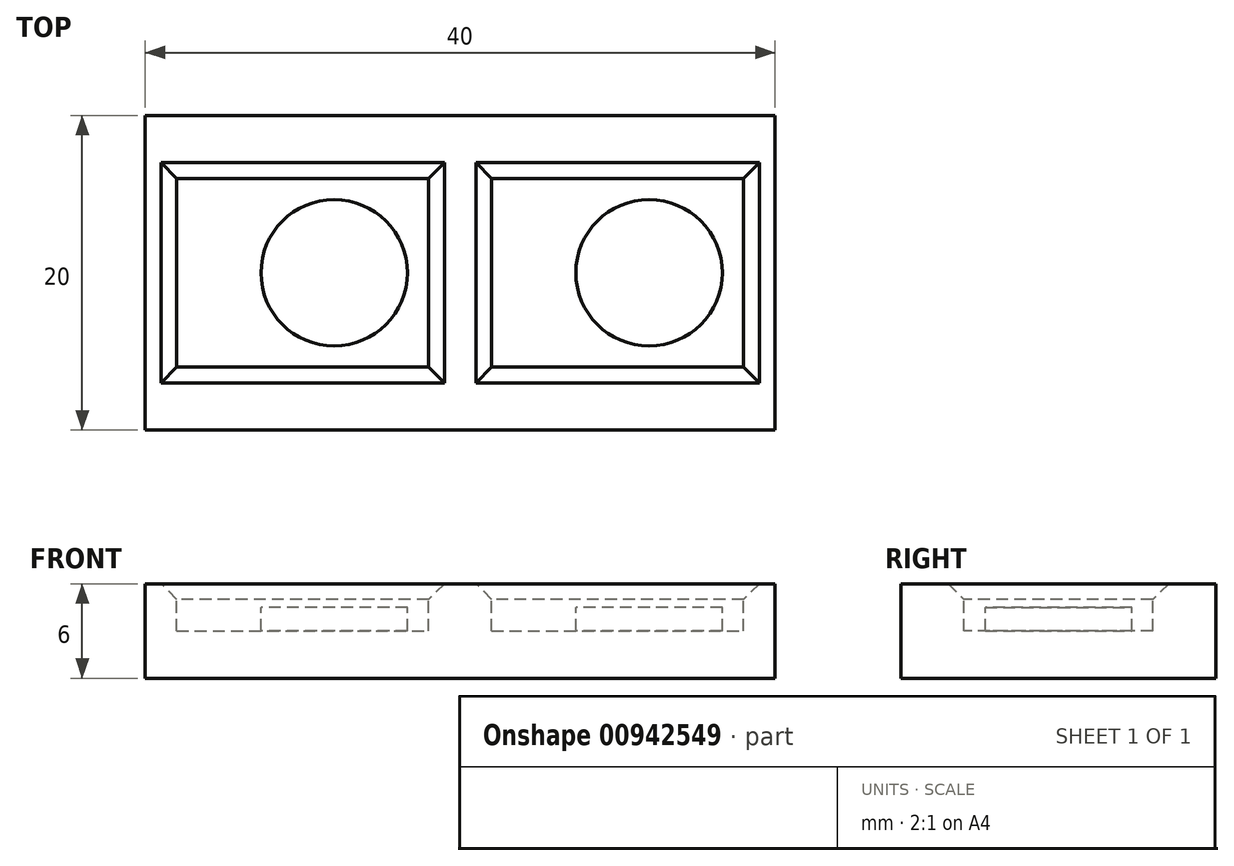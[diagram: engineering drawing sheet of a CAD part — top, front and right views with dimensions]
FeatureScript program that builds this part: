
annotation { "Feature Type Name" : "Feature", "Feature Type Description" : "" }
export const myFeature = defineFeature(function(context is Context, id is Id, definition is map)
    precondition{}
    {
        {
            var Q0;
            Q0=qCreatedBy(makeId("Top.planeOp"),FACE);
            var sketch = newSketch(context, id + "F0", { "sketchPlane" : qUnion([Q0])});
            skLineSegment(sketch, "E0.bottom", {"start": v(0, 0) * mm, "end": v(40, 0) * mm});
            skLineSegment(sketch, "E0.top", {"start": v(0, 20) * mm, "end": v(40, 20) * mm});
            skLineSegment(sketch, "E0.left", {"start": v(0, 0) * mm, "end": v(0, 20) * mm});
            skLineSegment(sketch, "E0.right", {"start": v(40, 0) * mm, "end": v(40, 20) * mm});
            skSolve(sketch);
        }
        {
            var Q0;
            Q0=makeQuery(id+"F0.imprint","IMPRINT",FACE,{"disambiguationData":[TD([[makeQuery(id+"F0.imprint","IMPRINT",EDGE,{"derivedFrom":sQuery(id+"F0.wireOp",EDGE,"E0.bottom")}),1.0]])]});
            extrude(context, id + "F1", {"entities" : qUnion([Q0]), "depth" : 6 * mm, "offsetDistance" : 25 * mm});
        }
        {
            var Q0;
            Q0=makeQuery(id+"F1.opExtrude","CAP_FACE",FACE,{"disambiguationData":[OSD([sQuery(id+"F0.wireOp",EDGE,"E0.bottom"),sQuery(id+"F0.wireOp",EDGE,"E0.top"),sQuery(id+"F0.wireOp",EDGE,"E0.left"),sQuery(id+"F0.wireOp",EDGE,"E0.right")])],"isStart":false});
            var sketch = newSketch(context, id + "F2", { "sketchPlane" : qUnion([Q0])});
            skLineSegment(sketch, "E1.bottom", {"start": v(2, 16) * mm, "end": v(18, 16) * mm});
            skLineSegment(sketch, "E1.top", {"start": v(2, 4) * mm, "end": v(18, 4) * mm});
            skLineSegment(sketch, "E1.left", {"start": v(2, 16) * mm, "end": v(2, 4) * mm});
            skLineSegment(sketch, "E1.right", {"start": v(18, 16) * mm, "end": v(18, 4) * mm});
            skLineSegment(sketch, "E2.bottom", {"start": v(22, 16) * mm, "end": v(38, 16) * mm});
            skLineSegment(sketch, "E2.top", {"start": v(22, 4) * mm, "end": v(38, 4) * mm});
            skLineSegment(sketch, "E2.left", {"start": v(22, 16) * mm, "end": v(22, 4) * mm});
            skLineSegment(sketch, "E2.right", {"start": v(38, 16) * mm, "end": v(38, 4) * mm});
            skCircle(sketch, "E3", {"center": v(12, 10) * mm, "radius": 4.65 * mm});
            skCircle(sketch, "E4", {"center": v(32, 10) * mm, "radius": 4.65 * mm});
            skSolve(sketch);
        }
        {
            var Q0;
            Q0=makeQuery(id+"F2.imprint","IMPRINT",FACE,{"disambiguationData":[TD([[makeQuery(id+"F2.imprint","IMPRINT",EDGE,{"derivedFrom":sQuery(id+"F2.wireOp",EDGE,"E1.bottom")}),-1.0]])]});
            var Q1;
            Q1=makeQuery(id+"F2.imprint","IMPRINT",FACE,{"disambiguationData":[TD([[makeQuery(id+"F2.imprint","IMPRINT",EDGE,{"derivedFrom":sQuery(id+"F2.wireOp",EDGE,"E2.bottom")}),-1.0]])]});
            extrude(context, id + "F3", {"entities" : qUnion([Q0, Q1]), "operationType" : NewBodyOperationType.REMOVE, "oppositeDirection" : true, "depth" : 3 * mm, "offsetDistance" : 25 * mm});
        }
        {
            var Q0;
            Q0=makeQuery(id+"F3.boolean.opBoolean","SPLIT",FACE,{"disambiguationData":[TD([makeQuery(id+"F3.opExtrude","SWEPT_FACE",FACE,{"disambiguationData":[OSD([sQuery(id+"F2.wireOp",EDGE,"E3")])]})])],"derivedFrom":makeQuery(id+"F1.opExtrude","CAP_FACE",FACE,{"disambiguationData":[OSD([sQuery(id+"F0.wireOp",EDGE,"E0.bottom"),sQuery(id+"F0.wireOp",EDGE,"E0.top"),sQuery(id+"F0.wireOp",EDGE,"E0.left"),sQuery(id+"F0.wireOp",EDGE,"E0.right")])],"isStart":false})});
            var Q1;
            Q1=makeQuery(id+"F3.boolean.opBoolean","SPLIT",FACE,{"disambiguationData":[TD([makeQuery(id+"F3.opExtrude","SWEPT_FACE",FACE,{"disambiguationData":[OSD([sQuery(id+"F2.wireOp",EDGE,"E4")])]})])],"derivedFrom":makeQuery(id+"F1.opExtrude","CAP_FACE",FACE,{"disambiguationData":[OSD([sQuery(id+"F0.wireOp",EDGE,"E0.bottom"),sQuery(id+"F0.wireOp",EDGE,"E0.top"),sQuery(id+"F0.wireOp",EDGE,"E0.left"),sQuery(id+"F0.wireOp",EDGE,"E0.right")])],"isStart":false})});
            extrude(context, id + "F4", {"entities" : qUnion([Q0, Q1]), "operationType" : NewBodyOperationType.REMOVE, "oppositeDirection" : true, "depth" : 1.5 * mm, "offsetDistance" : 25 * mm});
        }
        {
            var Q0;
            Q0=makeQuery(id+"F3.boolean.opBoolean","COPY",EDGE,{"derivedFrom":makeQuery(id+"F3.opExtrude","CAP_EDGE",EDGE,{"disambiguationData":[OSD([sQuery(id+"F2.wireOp",EDGE,"E1.bottom")])],"isStart":true})});
            var Q1;
            Q1=makeQuery(id+"F3.boolean.opBoolean","COPY",EDGE,{"derivedFrom":makeQuery(id+"F3.opExtrude","CAP_EDGE",EDGE,{"disambiguationData":[OSD([sQuery(id+"F2.wireOp",EDGE,"E1.right")])],"isStart":true})});
            var Q2;
            Q2=makeQuery(id+"F3.boolean.opBoolean","COPY",EDGE,{"derivedFrom":makeQuery(id+"F3.opExtrude","CAP_EDGE",EDGE,{"disambiguationData":[OSD([sQuery(id+"F2.wireOp",EDGE,"E1.top")])],"isStart":true})});
            var Q3;
            Q3=makeQuery(id+"F3.boolean.opBoolean","COPY",EDGE,{"derivedFrom":makeQuery(id+"F3.opExtrude","CAP_EDGE",EDGE,{"disambiguationData":[OSD([sQuery(id+"F2.wireOp",EDGE,"E1.left")])],"isStart":true})});
            var Q4;
            Q4=makeQuery(id+"F3.boolean.opBoolean","COPY",EDGE,{"derivedFrom":makeQuery(id+"F3.opExtrude","CAP_EDGE",EDGE,{"disambiguationData":[OSD([sQuery(id+"F2.wireOp",EDGE,"E2.left")])],"isStart":true})});
            var Q5;
            Q5=makeQuery(id+"F3.boolean.opBoolean","COPY",EDGE,{"derivedFrom":makeQuery(id+"F3.opExtrude","CAP_EDGE",EDGE,{"disambiguationData":[OSD([sQuery(id+"F2.wireOp",EDGE,"E2.bottom")])],"isStart":true})});
            var Q6;
            Q6=makeQuery(id+"F3.boolean.opBoolean","COPY",EDGE,{"derivedFrom":makeQuery(id+"F3.opExtrude","CAP_EDGE",EDGE,{"disambiguationData":[OSD([sQuery(id+"F2.wireOp",EDGE,"E2.right")])],"isStart":true})});
            var Q7;
            Q7=makeQuery(id+"F3.boolean.opBoolean","COPY",EDGE,{"derivedFrom":makeQuery(id+"F3.opExtrude","CAP_EDGE",EDGE,{"disambiguationData":[OSD([sQuery(id+"F2.wireOp",EDGE,"E2.top")])],"isStart":true})});
            chamfer(context, id + "F5", {"entities" : qUnion([Q0, Q1, Q2, Q3, Q4, Q5, Q6, Q7]), "width" : 1 * mm, "tangentPropagation" : true});
        }
    });
